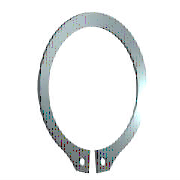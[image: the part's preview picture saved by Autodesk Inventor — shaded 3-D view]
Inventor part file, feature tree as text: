
AUTODESK INVENTOR PART (.ipt)
format: ipt  version: 2015 (Build 190159000, 159)  size: 151,040 bytes
history: native  units: mm (DEFAULTED — no unit token found)
features: sketch x2
ambient origin geometry x8: Origin, YZ Plane, XZ Plane, XY Plane, X Axis, Y Axis, Z Axis, Center Point
bodies: Solid1 (feature_tree)
feature tree (2):
  sketch  "草图2"  dims[d0=0.0mm]
  sketch  "草图3"  dims[d2=1.9mm d4=0.55mm d6=2.2mm d8=1.65mm d10=3.3mm d12=0.44mm d14=0.3mm d15=1.2mm d16=1.3mm d17=0.0mm d18=1.1mm d20=0.99mm d22=0.99mm d24=1.0mm d26=0.13mm d27=0.0mm d28=28.35mm d32=3.6mm d34=5.0mm d35=1.666667mm d36=2.0mm d37=2.5mm d47=5.466667mm d48=3.6mm d49=1.0mm d51=0.0mm d52=0.0mm d53=0.0mm d54=0.0mm]
